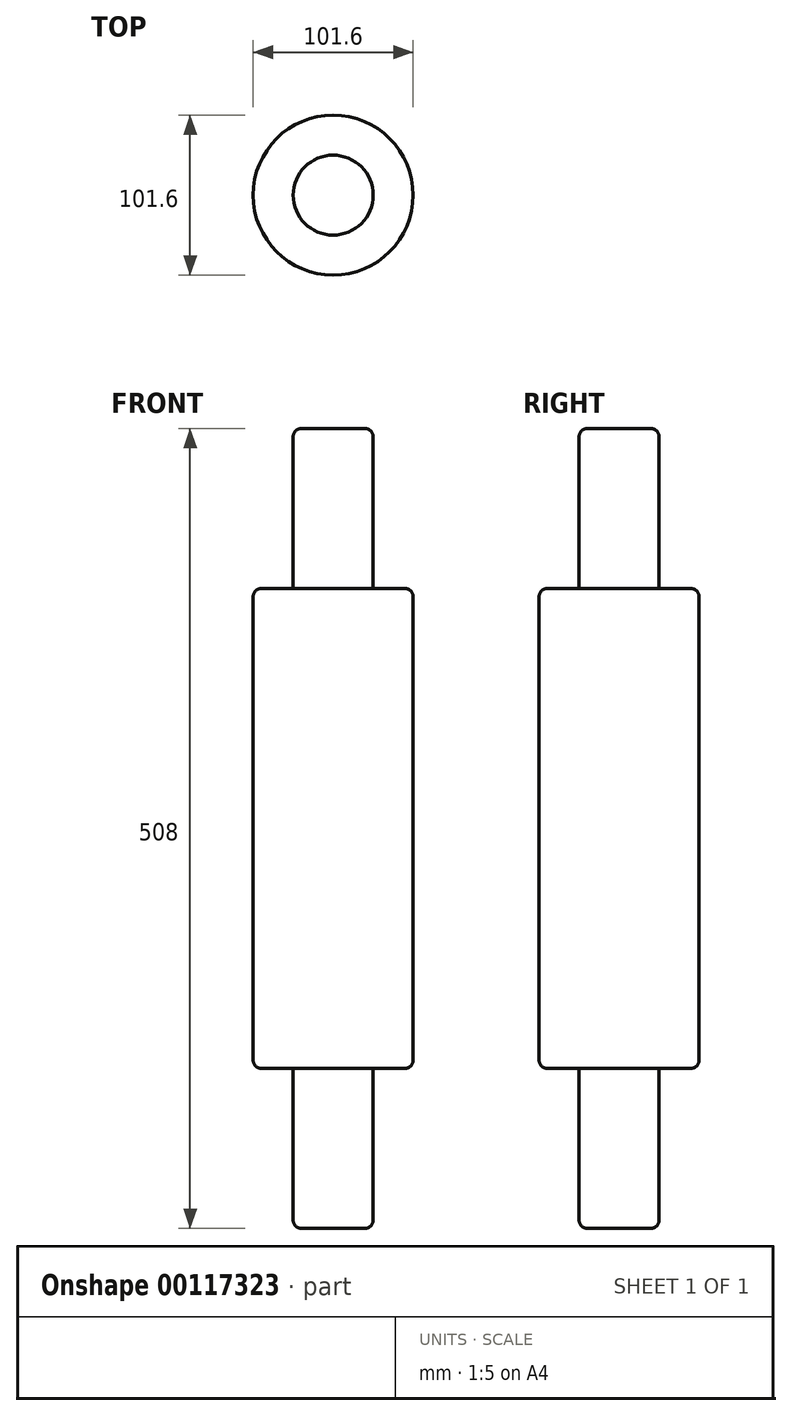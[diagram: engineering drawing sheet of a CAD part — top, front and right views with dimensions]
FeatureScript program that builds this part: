
annotation { "Feature Type Name" : "Feature", "Feature Type Description" : "" }
export const myFeature = defineFeature(function(context is Context, id is Id, definition is map)
    precondition{}
    {
        {
            var Q0;
            Q0=qCreatedBy(makeId("Top.planeOp"),FACE);
            var sketch = newSketch(context, id + "F0", { "sketchPlane" : qUnion([Q0])});
            skCircle(sketch, "E0", {"center": v(0, 0) * mm, "radius": 50.8 * mm});
            skSolve(sketch);
        }
        {
            var Q0;
            Q0=makeQuery(id+"F0.imprint","IMPRINT",FACE,{"disambiguationData":[TD([[makeQuery(id+"F0.imprint","IMPRINT",EDGE,{"derivedFrom":sQuery(id+"F0.wireOp",EDGE,"E0")}),1.0]])]});
            extrude(context, id + "F1", {"entities" : qUnion([Q0]), "depth" : 304.8 * mm});
        }
        {
            var Q0;
            Q0=makeQuery(id+"F1.opExtrude","CAP_FACE",FACE,{"disambiguationData":[OSD([sQuery(id+"F0.wireOp",EDGE,"E0")])],"isStart":false});
            fillet(context, id + "F2", {"entities" : qUnion([Q0]), "radius" : 5.08 * mm, "tangentPropagation" : true, "allowEdgeOverflow" : false});
        }
        {
            var Q0;
            Q0=makeQuery(id+"F1.opExtrude","CAP_FACE",FACE,{"disambiguationData":[OSD([sQuery(id+"F0.wireOp",EDGE,"E0")])],"isStart":true});
            fillet(context, id + "F3", {"entities" : qUnion([Q0]), "radius" : 5.08 * mm, "tangentPropagation" : true, "allowEdgeOverflow" : false});
        }
        {
            var Q0;
            Q0=makeQuery(id+"F1.opExtrude","CAP_FACE",FACE,{"disambiguationData":[OSD([sQuery(id+"F0.wireOp",EDGE,"E0")])],"isStart":false});
            var sketch = newSketch(context, id + "F4", { "sketchPlane" : qUnion([Q0])});
            skCircle(sketch, "E1", {"center": v(0, 0) * mm, "radius": 25.4 * mm});
            skSolve(sketch);
        }
        {
            var Q0;
            Q0=makeQuery(id+"F4.imprint","IMPRINT",FACE,{"disambiguationData":[TD([[makeQuery(id+"F4.imprint","IMPRINT",EDGE,{"derivedFrom":sQuery(id+"F4.wireOp",EDGE,"E1")}),1.0]])]});
            extrude(context, id + "F5", {"entities" : qUnion([Q0]), "operationType" : NewBodyOperationType.ADD, "depth" : 101.6 * mm});
        }
        {
            var Q0;
            Q0=makeQuery(id+"F5.opExtrude","CAP_FACE",FACE,{"disambiguationData":[OSD([sQuery(id+"F4.wireOp",EDGE,"E1")])],"isStart":false});
            fillet(context, id + "F6", {"entities" : qUnion([Q0]), "radius" : 5.08 * mm, "tangentPropagation" : true, "allowEdgeOverflow" : false});
        }
        {
            var Q0;
            Q0=makeQuery(id+"F1.opExtrude","CAP_FACE",FACE,{"disambiguationData":[OSD([sQuery(id+"F0.wireOp",EDGE,"E0")])],"isStart":true});
            var sketch = newSketch(context, id + "F7", { "sketchPlane" : qUnion([Q0])});
            skCircle(sketch, "E2", {"center": v(0, 0) * mm, "radius": 25.4 * mm});
            skSolve(sketch);
        }
        {
            var Q0;
            Q0=makeQuery(id+"F7.imprint","IMPRINT",FACE,{"disambiguationData":[TD([[makeQuery(id+"F7.imprint","IMPRINT",EDGE,{"derivedFrom":sQuery(id+"F7.wireOp",EDGE,"E2")}),1.0]])]});
            extrude(context, id + "F8", {"entities" : qUnion([Q0]), "operationType" : NewBodyOperationType.ADD, "depth" : 101.6 * mm});
        }
        {
            var Q0;
            Q0=makeQuery(id+"F8.opExtrude","CAP_FACE",FACE,{"disambiguationData":[OSD([sQuery(id+"F7.wireOp",EDGE,"E2")])],"isStart":false});
            fillet(context, id + "F9", {"entities" : qUnion([Q0]), "radius" : 5.08 * mm, "tangentPropagation" : true, "allowEdgeOverflow" : false});
        }
    });
